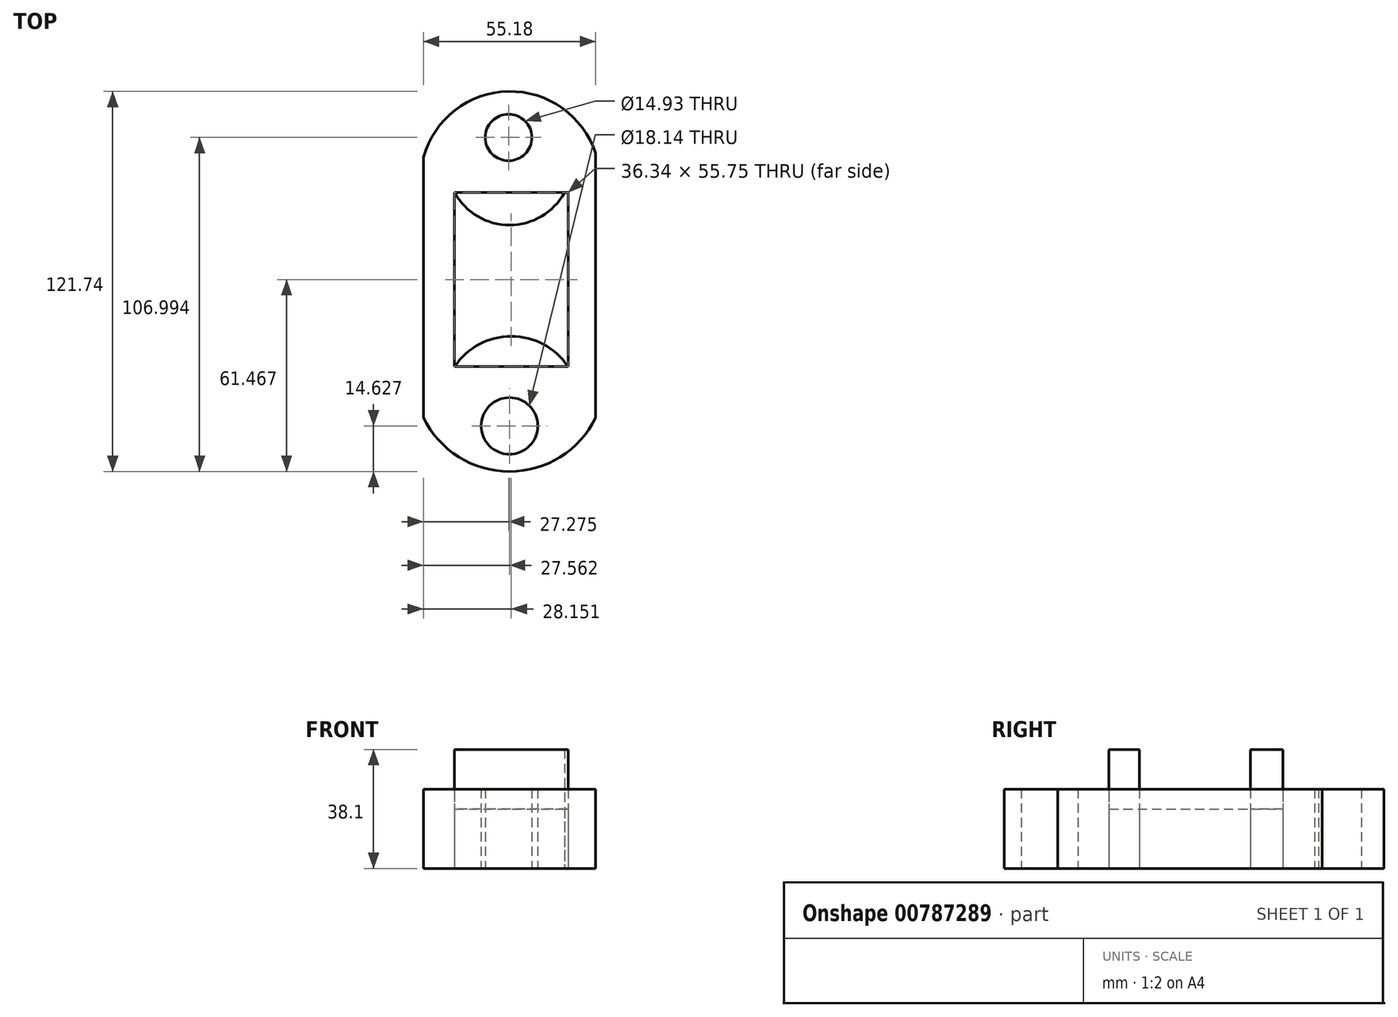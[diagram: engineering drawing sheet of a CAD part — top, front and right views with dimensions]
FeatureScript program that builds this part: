
annotation { "Feature Type Name" : "Feature", "Feature Type Description" : "" }
export const myFeature = defineFeature(function(context is Context, id is Id, definition is map)
    precondition{}
    {
        {
            var Q0;
            Q0=qCreatedBy(makeId("Top.planeOp"),FACE);
            var sketch = newSketch(context, id + "F0", { "sketchPlane" : qUnion([Q0])});
            skArc(sketch, "E0", {"start": v(33.43, 51.25) * mm, "mid": v(5.4, 71.09) * mm, "end": v(-21.75, 50.08) * mm});
            skLineSegment(sketch, "E1", {"start": v(-21.75, 50.08) * mm, "end": v(-21.75, -33.43) * mm});
            skLineSegment(sketch, "E2", {"start": v(33.43, 51.25) * mm, "end": v(33.43, -33.43) * mm});
            skArc(sketch, "E3", {"start": v(-21.75, -33.43) * mm, "mid": v(5.84, -50.65) * mm, "end": v(33.43, -33.43) * mm});
            skCircle(sketch, "E4", {"center": v(5.53, 56.34) * mm, "radius": 7.46 * mm});
            skCircle(sketch, "E5", {"center": v(5.81, -36.02) * mm, "radius": 9.07 * mm});
            skLineSegment(sketch, "E6", {"start": v(-11.77, 38.7) * mm, "end": v(24.57, 38.7) * mm});
            skLineSegment(sketch, "E7", {"start": v(24.57, -17.06) * mm, "end": v(-11.77, -17.06) * mm});
            skLineSegment(sketch, "E8", {"start": v(-11.77, -17.06) * mm, "end": v(-11.77, 38.7) * mm});
            skLineSegment(sketch, "E9", {"start": v(24.57, 38.7) * mm, "end": v(24.57, -17.06) * mm});
            skArc(sketch, "E10", {"start": v(-11.77, 38.7) * mm, "mid": v(7.15, 28.33) * mm, "end": v(24.57, 41.06) * mm});
            skArc(sketch, "E11", {"start": v(24.57, -17.06) * mm, "mid": v(6.4, -7.35) * mm, "end": v(-11.77, -17.06) * mm});
            skSolve(sketch);
        }
        {
            var Q0;
            {var subQ0=sQuery(id+"F0.wireOp",EDGE,"E10");var subQ1=sQuery(id+"F0.wireOp",EDGE,"E6");var subQ3=makeQuery(id+"F0.imprint","INTERSECT",VERTEX,{"derivedFrom":[subQ1,subQ0]});Q0=makeQuery(id+"F0.imprint","IMPRINT",FACE,{"disambiguationData":[TD([[makeQuery(id+"F0.imprint","IMPRINT",EDGE,{"disambiguationData":[TD([[subQ3,1.0]])],"derivedFrom":subQ1}),-1.0]])]});}
            var Q1;
            Q1=makeQuery(id+"F0.imprint","IMPRINT",FACE,{"disambiguationData":[TD([[makeQuery(id+"F0.imprint","IMPRINT",EDGE,{"derivedFrom":sQuery(id+"F0.wireOp",EDGE,"E7")}),-1.0]])]});
            extrude(context, id + "F1", {"entities" : qUnion([Q0, Q1]), "depth" : 38.1 * mm, "offsetDistance" : 25.4 * mm});
        }
        {
            var Q0;
            Q0=makeQuery(id+"F0.imprint","IMPRINT",FACE,{"disambiguationData":[TD([[makeQuery(id+"F0.imprint","IMPRINT",EDGE,{"derivedFrom":sQuery(id+"F0.wireOp",EDGE,"E0")}),1.0]])]});
            extrude(context, id + "F2", {"entities" : qUnion([Q0]), "depth" : 25.4 * mm, "offsetDistance" : 25.4 * mm});
        }
        {
            var Q0;
            {var subQ1=sQuery(id+"F0.wireOp",EDGE,"E8");Q0=makeQuery(id+"F0.imprint","IMPRINT",FACE,{"disambiguationData":[TD([[makeQuery(id+"F0.imprint","IMPRINT",EDGE,{"derivedFrom":subQ1}),-1.0]])]});}
            extrude(context, id + "F3", {"entities" : qUnion([Q0]), "depth" : 19.05 * mm, "offsetDistance" : 25.4 * mm});
        }
    });
